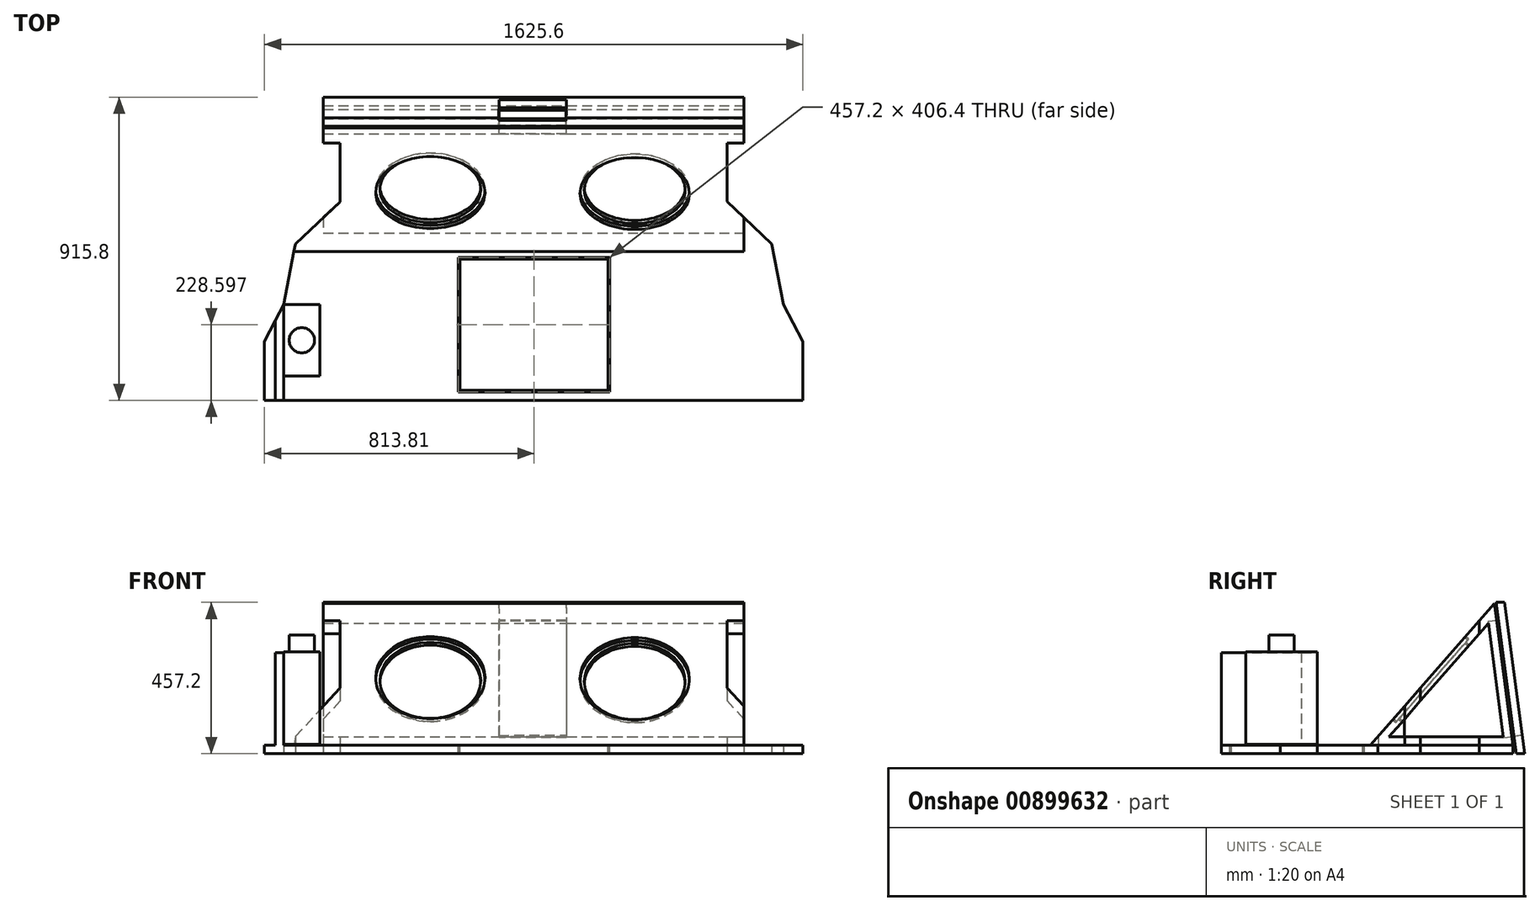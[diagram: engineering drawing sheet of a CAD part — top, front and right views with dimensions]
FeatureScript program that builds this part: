
annotation { "Feature Type Name" : "Feature", "Feature Type Description" : "" }
export const myFeature = defineFeature(function(context is Context, id is Id, definition is map)
    precondition{}
    {
        {
            var Q0;
            Q0=qCreatedBy(makeId("Top.planeOp"),FACE);
            var sketch = newSketch(context, id + "F0", { "sketchPlane" : qUnion([Q0])});
            skLineSegment(sketch, "E0.bottom", {"start": v(-636, 381) * mm, "end": v(634, 381) * mm});
            skLineSegment(sketch, "E1", {"start": v(-636, -498.3) * mm, "end": v(-813.8, -498.3) * mm});
            skLineSegment(sketch, "E2", {"start": v(634, -498.3) * mm, "end": v(811.8, -498.3) * mm});
            skLineSegment(sketch, "E3", {"start": v(-636, -498.3) * mm, "end": v(634, -498.3) * mm});
            skLineSegment(sketch, "E4", {"start": v(-813.8, -498.3) * mm, "end": v(-813.8, -320.5) * mm});
            skLineSegment(sketch, "E5", {"start": v(-636, 381) * mm, "end": v(-636, 279.4) * mm});
            skLineSegment(sketch, "E6", {"start": v(-636, 279.4) * mm, "end": v(-585.2, 279.4) * mm});
            skLineSegment(sketch, "E7", {"start": v(-585.2, 279.4) * mm, "end": v(-585.2, 101.6) * mm});
            skLineSegment(sketch, "E8", {"start": v(-585.2, 101.6) * mm, "end": v(-720.27, -26) * mm});
            skLineSegment(sketch, "E9", {"start": v(634, 381) * mm, "end": v(634, 279.4) * mm});
            skLineSegment(sketch, "E10", {"start": v(634, 279.4) * mm, "end": v(583.2, 279.4) * mm});
            skLineSegment(sketch, "E11", {"start": v(583.2, 279.4) * mm, "end": v(583.2, 101.6) * mm});
            skLineSegment(sketch, "E12", {"start": v(583.2, 101.6) * mm, "end": v(718.25, -26) * mm});
            skLineSegment(sketch, "E13", {"start": v(811.8, -320.5) * mm, "end": v(811.8, -498.3) * mm});
            skLineSegment(sketch, "E14", {"start": v(-813.8, -320.5) * mm, "end": v(-755.4, -208.82) * mm});
            skLineSegment(sketch, "E15", {"start": v(-755.4, -208.82) * mm, "end": v(-720.27, -26) * mm});
            skLineSegment(sketch, "E16", {"start": v(811.8, -320.5) * mm, "end": v(753.38, -208.82) * mm});
            skLineSegment(sketch, "E17", {"start": v(753.38, -208.82) * mm, "end": v(718.25, -26) * mm});
            skSolve(sketch);
        }
        {
            var Q0;
            Q0 = qSketchRegion(id + "F0", true);
            extrude(context, id + "F1", {"entities" : qUnion([Q0]), "depth" : 25.4 * mm, "offsetDistance" : 25.4 * mm});
        }
        {
            var Q0;
            Q0=makeQuery(id+"F1.opExtrude","SWEPT_FACE",FACE,{"disambiguationData":[OSD([sQuery(id+"F0.wireOp",EDGE,"E9")])]});
            var sketch = newSketch(context, id + "F2", { "sketchPlane" : qUnion([Q0])});
            skPoint(sketch, "E18.endSnap0", {"position": v(330.2, 0) * mm});
            skLineSegment(sketch, "E19", {"start": v(330.2, 457.2) * mm, "end": v(355.6, 457.2) * mm});
            skLineSegment(sketch, "E20", {"start": v(355.6, 457.2) * mm, "end": v(417.5, 0) * mm});
            skLineSegment(sketch, "E21", {"start": v(417.5, 0) * mm, "end": v(392.1, 0) * mm});
            skLineSegment(sketch, "E22", {"start": v(330.2, 457.2) * mm, "end": v(392.1, 0) * mm});
            skSolve(sketch);
        }
        {
            var Q0;
            Q0 = qSketchRegion(id + "F2", true);
            extrude(context, id + "F3", {"entities" : qUnion([Q0]), "oppositeDirection" : true, "depth" : 1270 * mm, "offsetDistance" : 25.4 * mm});
        }
        {
            var Q0;
            Q0=makeQuery(id+"F3.opExtrude","SWEPT_FACE",FACE,{"disambiguationData":[OSD([sQuery(id+"F2.wireOp",EDGE,"E22")])]});
            var sketch = newSketch(context, id + "F4", { "sketchPlane" : qUnion([Q0])});
            skLineSegment(sketch, "E23.bottom", {"start": v(97.29, 406.64) * mm, "end": v(-105.91, 406.4) * mm});
            skLineSegment(sketch, "E23.left", {"start": v(97.29, 406.64) * mm, "end": v(97.78, 0.24) * mm});
            skLineSegment(sketch, "E23.right", {"start": v(-105.91, 406.4) * mm, "end": v(-105.42, 0) * mm});
            skLineSegment(sketch, "E24", {"start": v(-105.42, 0) * mm, "end": v(97.78, 0.24) * mm});
            skLineSegment(sketch, "E25", {"start": v(-4.32, 408.76) * mm, "end": v(-4.32, -52.62) * mm});
            skSolve(sketch);
        }
        {
            var Q0;
            Q0=makeQuery(id+"F4.imprint","IMPRINT",FACE,{"disambiguationData":[TD([[makeQuery(id+"F4.imprint","IMPRINT",EDGE,{"derivedFrom":sQuery(id+"F4.wireOp",EDGE,"E23.bottom")}),1.0]])]});
            extrude(context, id + "F5", {"entities" : qUnion([Q0]), "operationType" : NewBodyOperationType.REMOVE, "oppositeDirection" : true, "depth" : 25.4 * mm, "offsetDistance" : 25.4 * mm});
        }
        {
            var Q0;
            Q0=makeQuery(id+"F1.opExtrude","CAP_FACE",FACE,{"disambiguationData":[OSD([sQuery(id+"F0.wireOp",EDGE,"E0.bottom"),sQuery(id+"F0.wireOp",EDGE,"E1"),sQuery(id+"F0.wireOp",EDGE,"E2"),sQuery(id+"F0.wireOp",EDGE,"E3"),sQuery(id+"F0.wireOp",EDGE,"E4"),sQuery(id+"F0.wireOp",EDGE,"E5"),sQuery(id+"F0.wireOp",EDGE,"E6"),sQuery(id+"F0.wireOp",EDGE,"E7"),sQuery(id+"F0.wireOp",EDGE,"E8"),sQuery(id+"F0.wireOp",EDGE,"E9"),sQuery(id+"F0.wireOp",EDGE,"E10"),sQuery(id+"F0.wireOp",EDGE,"E11"),sQuery(id+"F0.wireOp",EDGE,"E12"),sQuery(id+"F0.wireOp",EDGE,"E13"),sQuery(id+"F0.wireOp",EDGE,"E14"),sQuery(id+"F0.wireOp",EDGE,"E15"),sQuery(id+"F0.wireOp",EDGE,"E16"),sQuery(id+"F0.wireOp",EDGE,"E17")])],"isStart":false});
            var sketch = newSketch(context, id + "F6", { "sketchPlane" : qUnion([Q0])});
            skLineSegment(sketch, "E26.bottom", {"start": v(-228.6, -66.5) * mm, "end": v(228.6, -66.5) * mm});
            skLineSegment(sketch, "E26.top", {"start": v(-228.6, -472.9) * mm, "end": v(228.6, -472.9) * mm});
            skLineSegment(sketch, "E26.left", {"start": v(-228.6, -66.5) * mm, "end": v(-228.6, -472.9) * mm});
            skLineSegment(sketch, "E26.right", {"start": v(228.6, -66.5) * mm, "end": v(228.6, -472.9) * mm});
            skSolve(sketch);
        }
        {
            var Q0;
            Q0 = qSketchRegion(id + "F6", true);
            extrude(context, id + "F7", {"entities" : qUnion([Q0]), "operationType" : NewBodyOperationType.REMOVE, "oppositeDirection" : true, "depth" : 25.4 * mm, "offsetDistance" : 25.4 * mm});
        }
        {
            var Q0;
            Q0=makeQuery(id+"F1.opExtrude","CAP_FACE",FACE,{"disambiguationData":[OSD([sQuery(id+"F0.wireOp",EDGE,"E0.bottom"),sQuery(id+"F0.wireOp",EDGE,"E1"),sQuery(id+"F0.wireOp",EDGE,"E2"),sQuery(id+"F0.wireOp",EDGE,"E3"),sQuery(id+"F0.wireOp",EDGE,"E4"),sQuery(id+"F0.wireOp",EDGE,"E5"),sQuery(id+"F0.wireOp",EDGE,"E6"),sQuery(id+"F0.wireOp",EDGE,"E7"),sQuery(id+"F0.wireOp",EDGE,"E8"),sQuery(id+"F0.wireOp",EDGE,"E9"),sQuery(id+"F0.wireOp",EDGE,"E10"),sQuery(id+"F0.wireOp",EDGE,"E11"),sQuery(id+"F0.wireOp",EDGE,"E12"),sQuery(id+"F0.wireOp",EDGE,"E13"),sQuery(id+"F0.wireOp",EDGE,"E14"),sQuery(id+"F0.wireOp",EDGE,"E15"),sQuery(id+"F0.wireOp",EDGE,"E16"),sQuery(id+"F0.wireOp",EDGE,"E17")])],"isStart":false});
            var sketch = newSketch(context, id + "F8", { "sketchPlane" : qUnion([Q0])});
            skLineSegment(sketch, "E27.bottom", {"start": v(223.52, -71.57) * mm, "end": v(-223.52, -71.57) * mm});
            skLineSegment(sketch, "E27.top", {"start": v(223.52, -467.81) * mm, "end": v(-223.52, -467.81) * mm});
            skLineSegment(sketch, "E27.left", {"start": v(223.52, -71.57) * mm, "end": v(223.52, -467.81) * mm});
            skLineSegment(sketch, "E27.right", {"start": v(-223.52, -71.57) * mm, "end": v(-223.52, -467.81) * mm});
            skSolve(sketch);
        }
        {
            var Q0;
            Q0 = qSketchRegion(id + "F8", true);
            extrude(context, id + "F9", {"entities" : qUnion([Q0]), "oppositeDirection" : true, "depth" : 25.4 * mm, "offsetDistance" : 25.4 * mm});
        }
        {
            var Q0;
            Q0=makeQuery(id+"F1.opExtrude","SWEPT_FACE",FACE,{"disambiguationData":[OSD([sQuery(id+"F0.wireOp",EDGE,"E9")])]});
            var sketch = newSketch(context, id + "F10", { "sketchPlane" : qUnion([Q0])});
            skLineSegment(sketch, "E28", {"start": v(381, 25.4) * mm, "end": v(324.97, 453.55) * mm});
            skLineSegment(sketch, "E29", {"start": v(324.97, 453.55) * mm, "end": v(-48.98, 25.4) * mm});
            skPoint(sketch, "E30", {"position": v(138, 239.47) * mm});
            skLineSegment(sketch, "E31", {"start": v(-48.98, 25.4) * mm, "end": v(381, 25.4) * mm});
            skLineSegment(sketch, "E32", {"start": v(138, 239.47) * mm, "end": v(381, 25.4) * mm});
            skSolve(sketch);
        }
        {
            var Q0;
            Q0 = qSketchRegion(id + "F10", true);
            extrude(context, id + "F11", {"entities" : qUnion([Q0]), "oppositeDirection" : true, "depth" : 1358.9 * mm, "offsetDistance" : 25.4 * mm});
        }
        {
            var Q0;
            Q0=makeQuery(id+"F11.opExtrude","SWEPT_FACE",FACE,{"disambiguationData":[OSD([sQuery(id+"F10.wireOp",EDGE,"E29")])]});
            var sketch = newSketch(context, id + "F12", { "sketchPlane" : qUnion([Q0])});
            skCircle(sketch, "E33", {"center": v(304.24, 253.86) * mm, "radius": 165.1 * mm});
            skCircle(sketch, "E34", {"center": v(-312.87, 258.14) * mm, "radius": 165.1 * mm});
            skSolve(sketch);
        }
        {
            var Q0;
            Q0 = qSketchRegion(id + "F12", true);
            extrude(context, id + "F13", {"entities" : qUnion([Q0]), "operationType" : NewBodyOperationType.REMOVE, "oppositeDirection" : true, "depth" : 12.7 * mm, "offsetDistance" : 25.4 * mm});
        }
        {
            var Q0;
            Q0=makeQuery(id+"F11.opExtrude","CAP_FACE",FACE,{"disambiguationData":[OSD([sQuery(id+"F10.wireOp",EDGE,"E28"),sQuery(id+"F10.wireOp",EDGE,"E29"),sQuery(id+"F10.wireOp",EDGE,"E31")])],"isStart":true});
            var sketch = newSketch(context, id + "F14", { "sketchPlane" : qUnion([Q0])});
            skLineSegment(sketch, "E35", {"start": v(307.09, 394.46) * mm, "end": v(6.93, 50.8) * mm});
            skLineSegment(sketch, "E36", {"start": v(6.93, 50.8) * mm, "end": v(352.06, 50.8) * mm});
            skLineSegment(sketch, "E37", {"start": v(307.09, 394.46) * mm, "end": v(352.06, 50.8) * mm});
            skSolve(sketch);
        }
        {
            var Q0;
            Q0 = qSketchRegion(id + "F14", true);
            extrude(context, id + "F15", {"entities" : qUnion([Q0]), "operationType" : NewBodyOperationType.REMOVE, "oppositeDirection" : true, "depth" : 1270 * mm, "offsetDistance" : 25.4 * mm});
        }
        {
            var Q0;
            Q0=makeQuery(id+"F11.opExtrude","SWEPT_FACE",FACE,{"disambiguationData":[OSD([sQuery(id+"F10.wireOp",EDGE,"E28")])]});
            var sketch = newSketch(context, id + "F16", { "sketchPlane" : qUnion([Q0])});
            skLineSegment(sketch, "E38", {"start": v(-97.35, 356.75) * mm, "end": v(105.85, 356.75) * mm});
            skLineSegment(sketch, "E39", {"start": v(-97.35, 356.75) * mm, "end": v(-97.35, 2.1) * mm});
            skLineSegment(sketch, "E40", {"start": v(105.42, 1.85) * mm, "end": v(105.85, 356.75) * mm});
            skLineSegment(sketch, "E41", {"start": v(-97.35, 2.1) * mm, "end": v(105.42, 1.85) * mm});
            skSolve(sketch);
        }
        {
            var Q0;
            Q0 = qSketchRegion(id + "F16", true);
            extrude(context, id + "F17", {"entities" : qUnion([Q0]), "operationType" : NewBodyOperationType.REMOVE, "oppositeDirection" : true, "depth" : 25.4 * mm, "offsetDistance" : 25.4 * mm});
        }
        {
            var Q0;
            Q0=makeQuery(id+"F13.boolean.opBoolean","COPY",FACE,{"derivedFrom":makeQuery(id+"F13.opExtrude","CAP_FACE",FACE,{"disambiguationData":[OSD([sQuery(id+"F12.wireOp",EDGE,"E33")])],"isStart":false})});
            var sketch = newSketch(context, id + "F18", { "sketchPlane" : qUnion([Q0])});
            skCircle(sketch, "E42", {"center": v(304.24, 253.86) * mm, "radius": 152.4 * mm});
            skCircle(sketch, "E43", {"center": v(-312.87, 258.14) * mm, "radius": 152.4 * mm});
            skSolve(sketch);
        }
        {
            var Q0;
            Q0 = qSketchRegion(id + "F18", true);
            extrude(context, id + "F19", {"entities" : qUnion([Q0]), "operationType" : NewBodyOperationType.REMOVE, "oppositeDirection" : true, "depth" : 25.4 * mm, "offsetDistance" : 25.4 * mm});
        }
        {
            var Q0;
            Q0=makeQuery(id+"F11.opExtrude","SWEPT_FACE",FACE,{"disambiguationData":[OSD([sQuery(id+"F10.wireOp",EDGE,"E31")])]});
            var sketch = newSketch(context, id + "F20", { "sketchPlane" : qUnion([Q0])});
            skLineSegment(sketch, "E44", {"start": v(583.2, -279.4) * mm, "end": v(634, -279.4) * mm});
            skLineSegment(sketch, "E45", {"start": v(583.2, -102.11) * mm, "end": v(583.2, -279.4) * mm});
            skLineSegment(sketch, "E46", {"start": v(583.2, -102.11) * mm, "end": v(634, -54.34) * mm});
            skLineSegment(sketch, "E47", {"start": v(634, -54.34) * mm, "end": v(634, -279.4) * mm});
            skLineSegment(sketch, "E48", {"start": v(-636, -279.4) * mm, "end": v(-585.2, -279.4) * mm});
            skLineSegment(sketch, "E49", {"start": v(-585.2, -101.6) * mm, "end": v(-585.2, -279.4) * mm});
            skPoint(sketch, "E50.orphan", {"position": v(-636, -279.4) * mm});
            skLineSegment(sketch, "E51", {"start": v(-585.2, -101.6) * mm, "end": v(-719.97, 25.7) * mm});
            skLineSegment(sketch, "E52", {"start": v(-636, -279.4) * mm, "end": v(-636, -381) * mm});
            skLineSegment(sketch, "E53", {"start": v(-636, -381) * mm, "end": v(-724.9, -381) * mm});
            skLineSegment(sketch, "E54", {"start": v(-724.9, -381) * mm, "end": v(-724.9, 48.98) * mm});
            skLineSegment(sketch, "E55", {"start": v(-724.9, 48.98) * mm, "end": v(-719.97, 25.7) * mm});
            skPoint(sketch, "E56.start.orphan", {"position": v(-722.63, -279.4) * mm});
            skSolve(sketch);
        }
        {
            var Q0;
            Q0 = qSketchRegion(id + "F20", true);
            extrude(context, id + "F21", {"entities" : qUnion([Q0]), "operationType" : NewBodyOperationType.REMOVE, "oppositeDirection" : true, "depth" : 508 * mm, "offsetDistance" : 25.4 * mm});
        }
        {
            var Q0;
            Q0=makeQuery(id+"F1.opExtrude","CAP_FACE",FACE,{"disambiguationData":[OSD([sQuery(id+"F0.wireOp",EDGE,"E0.bottom"),sQuery(id+"F0.wireOp",EDGE,"E1"),sQuery(id+"F0.wireOp",EDGE,"E2"),sQuery(id+"F0.wireOp",EDGE,"E3"),sQuery(id+"F0.wireOp",EDGE,"E4"),sQuery(id+"F0.wireOp",EDGE,"E5"),sQuery(id+"F0.wireOp",EDGE,"E6"),sQuery(id+"F0.wireOp",EDGE,"E7"),sQuery(id+"F0.wireOp",EDGE,"E8"),sQuery(id+"F0.wireOp",EDGE,"E9"),sQuery(id+"F0.wireOp",EDGE,"E10"),sQuery(id+"F0.wireOp",EDGE,"E11"),sQuery(id+"F0.wireOp",EDGE,"E12"),sQuery(id+"F0.wireOp",EDGE,"E13"),sQuery(id+"F0.wireOp",EDGE,"E14"),sQuery(id+"F0.wireOp",EDGE,"E15"),sQuery(id+"F0.wireOp",EDGE,"E16"),sQuery(id+"F0.wireOp",EDGE,"E17")])],"isStart":false});
            var sketch = newSketch(context, id + "F22", { "sketchPlane" : qUnion([Q0])});
            skLineSegment(sketch, "E57", {"start": v(-755.4, -208.82) * mm, "end": v(-755.4, -498.3) * mm});
            skLineSegment(sketch, "E58", {"start": v(-755.4, -498.3) * mm, "end": v(-780.8, -498.3) * mm});
            skLineSegment(sketch, "E59", {"start": v(-780.8, -498.3) * mm, "end": v(-780.8, -257.38) * mm});
            skLineSegment(sketch, "E60", {"start": v(-755.4, -208.82) * mm, "end": v(-780.8, -257.38) * mm});
            skPoint(sketch, "E61.orphan", {"position": v(-780.8, -208.82) * mm});
            skSolve(sketch);
        }
        {
            var Q0;
            Q0 = qSketchRegion(id + "F22", true);
            extrude(context, id + "F23", {"entities" : qUnion([Q0]), "operationType" : NewBodyOperationType.ADD, "depth" : 279.4 * mm, "offsetDistance" : 25.4 * mm});
        }
        {
            var Q0;
            Q0=makeQuery(id+"F23.opExtrude","SWEPT_FACE",FACE,{"disambiguationData":[OSD([sQuery(id+"F22.wireOp",EDGE,"E57")])]});
            var sketch = newSketch(context, id + "F24", { "sketchPlane" : qUnion([Q0])});
            skLineSegment(sketch, "E62.bottom", {"start": v(-424.72, 307.34) * mm, "end": v(-208.82, 307.34) * mm});
            skLineSegment(sketch, "E62.top", {"start": v(-424.72, 27.94) * mm, "end": v(-208.82, 27.94) * mm});
            skLineSegment(sketch, "E62.left", {"start": v(-424.72, 307.34) * mm, "end": v(-424.72, 27.94) * mm});
            skLineSegment(sketch, "E62.right", {"start": v(-208.82, 307.34) * mm, "end": v(-208.82, 27.94) * mm});
            skSolve(sketch);
        }
        {
            var Q0;
            Q0 = qSketchRegion(id + "F24", true);
            extrude(context, id + "F25", {"entities" : qUnion([Q0]), "operationType" : NewBodyOperationType.ADD, "depth" : 109.22 * mm, "offsetDistance" : 25.4 * mm});
        }
        {
            var Q0;
            Q0=makeQuery(id+"F25.opExtrude","SWEPT_FACE",FACE,{"disambiguationData":[OSD([sQuery(id+"F24.wireOp",EDGE,"E62.bottom")])]});
            var sketch = newSketch(context, id + "F26", { "sketchPlane" : qUnion([Q0])});
            skCircle(sketch, "E63", {"center": v(-700.8, -316.77) * mm, "radius": 38.1 * mm});
            skSolve(sketch);
        }
        {
            var Q0;
            Q0 = qSketchRegion(id + "F26", true);
            extrude(context, id + "F27", {"entities" : qUnion([Q0]), "operationType" : NewBodyOperationType.ADD, "depth" : 50.8 * mm, "offsetDistance" : 25.4 * mm});
        }
    });
